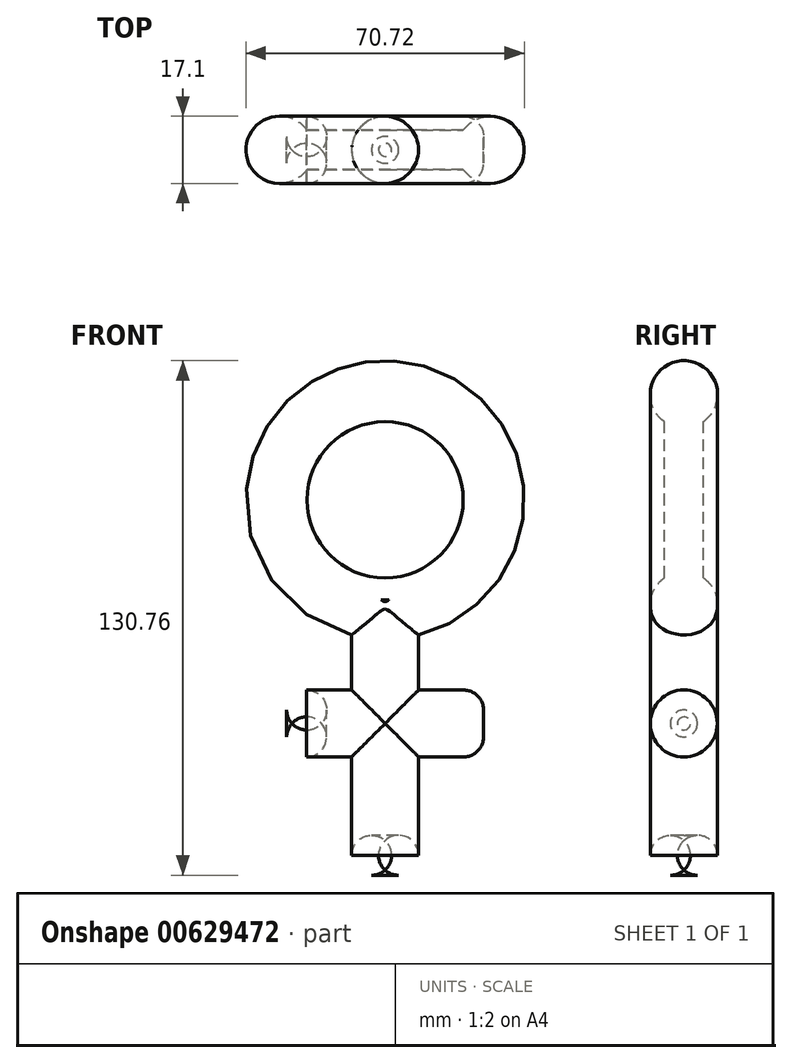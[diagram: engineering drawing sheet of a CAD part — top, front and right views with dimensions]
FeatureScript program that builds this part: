
annotation { "Feature Type Name" : "Feature", "Feature Type Description" : "" }
export const myFeature = defineFeature(function(context is Context, id is Id, definition is map)
    precondition{}
    {
        {
            var Q0;
            Q0=qCreatedBy(makeId("Right.planeOp"),FACE);
            var sketch = newSketch(context, id + "F0", { "sketchPlane" : qUnion([Q0])});
            skArc(sketch, "E0", {"start": v(4.96, 19.84) * mm, "mid": v(0, 35.36) * mm, "end": v(-4.96, 19.84) * mm});
            skLineSegment(sketch, "E1", {"start": v(4.96, 0) * mm, "end": v(4.96, 19.84) * mm});
            skLineSegment(sketch, "E2", {"start": v(4.96, 0) * mm, "end": v(0, 0) * mm});
            skLineSegment(sketch, "E3", {"start": v(0, 0) * mm, "end": v(0, 4.5) * mm});
            skLineSegment(sketch, "E4.MirrorCS", {"start": v(-4.96, 0) * mm, "end": v(-4.96, 19.84) * mm});
            skLineSegment(sketch, "E5.MirrorCS", {"start": v(-4.96, 0) * mm, "end": v(0, 0) * mm});
            skSolve(sketch);
        }
        {
            var Q0;
            Q0=makeQuery(id+"F0.imprint","IMPRINT",FACE,{"disambiguationData":[TD([[makeQuery(id+"F0.imprint","IMPRINT",EDGE,{"derivedFrom":sQuery(id+"F0.wireOp",EDGE,"E0")}),1.0]])]});
            var Q1;
            Q1=sQuery(id+"F0.wireOp",EDGE,"E5.MirrorCS");
            revolve(context, id + "F1", {"surfaceOperationType" : NewSurfaceOperationType.NEW, "entities" : qUnion([Q0]), "axis" : qUnion([Q1]), "revolveType" : RevolveType.FULL});
        }
        {
            var Q0;
            Q0=qCreatedBy(makeId("Top.planeOp"),FACE);
            cPlane(context, id + "F2", {"entities" : qUnion([Q0]), "cplaneType" : CPlaneType.OFFSET, "offset" : 25.4 * mm, "oppositeDirection" : true, "width" : 152.4 * mm, "height" : 152.4 * mm});
        }
        {
            var Q0;
            Q0=qCreatedBy(id+"F2.planeOp",FACE);
            var sketch = newSketch(context, id + "F3", { "sketchPlane" : qUnion([Q0])});
            skCircle(sketch, "E6", {"center": v(0, 0) * mm, "radius": 8.5 * mm});
            skSolve(sketch);
        }
        {
            var Q0;
            Q0 = qSketchRegion(id + "F3", true);
            extrude(context, id + "F4", {"entities" : qUnion([Q0]), "operationType" : NewBodyOperationType.ADD, "oppositeDirection" : true, "depth" : 70 * mm, "offsetDistance" : 25.4 * mm});
        }
        {
            var Q0;
            Q0=makeQuery(id+"F4.opExtrude","CAP_FACE",FACE,{"disambiguationData":[OSD([sQuery(id+"F3.wireOp",EDGE,"E6")])],"isStart":false});
            fillet(context, id + "F5", {"entities" : qUnion([Q0]), "radius" : 5.08 * mm, "tangentPropagation" : true, "allowEdgeOverflow" : false});
        }
        {
            var Q0;
            Q0=qCreatedBy(makeId("Right.planeOp"),FACE);
            var sketch = newSketch(context, id + "F6", { "sketchPlane" : qUnion([Q0])});
            skCircle(sketch, "E7", {"center": v(0, -56.82) * mm, "radius": 8.5 * mm});
            skSolve(sketch);
        }
        {
            var Q0;
            Q0 = qSketchRegion(id + "F6", true);
            extrude(context, id + "F7", {"entities" : qUnion([Q0]), "operationType" : NewBodyOperationType.ADD, "endBound" : BoundingType.SYMMETRIC, "oppositeDirection" : true, "depth" : 50 * mm, "offsetDistance" : 25.4 * mm});
        }
        {
            var Q0;
            Q0=makeQuery(id+"F7.opExtrude","CAP_FACE",FACE,{"disambiguationData":[OSD([sQuery(id+"F6.wireOp",EDGE,"E7")])],"isStart":false});
            var Q1;
            Q1=makeQuery(id+"F7.opExtrude","CAP_FACE",FACE,{"disambiguationData":[OSD([sQuery(id+"F6.wireOp",EDGE,"E7")])],"isStart":true});
            fillet(context, id + "F8", {"entities" : qUnion([Q0, Q1]), "radius" : 5.08 * mm, "tangentPropagation" : true, "allowEdgeOverflow" : false});
        }
    });
